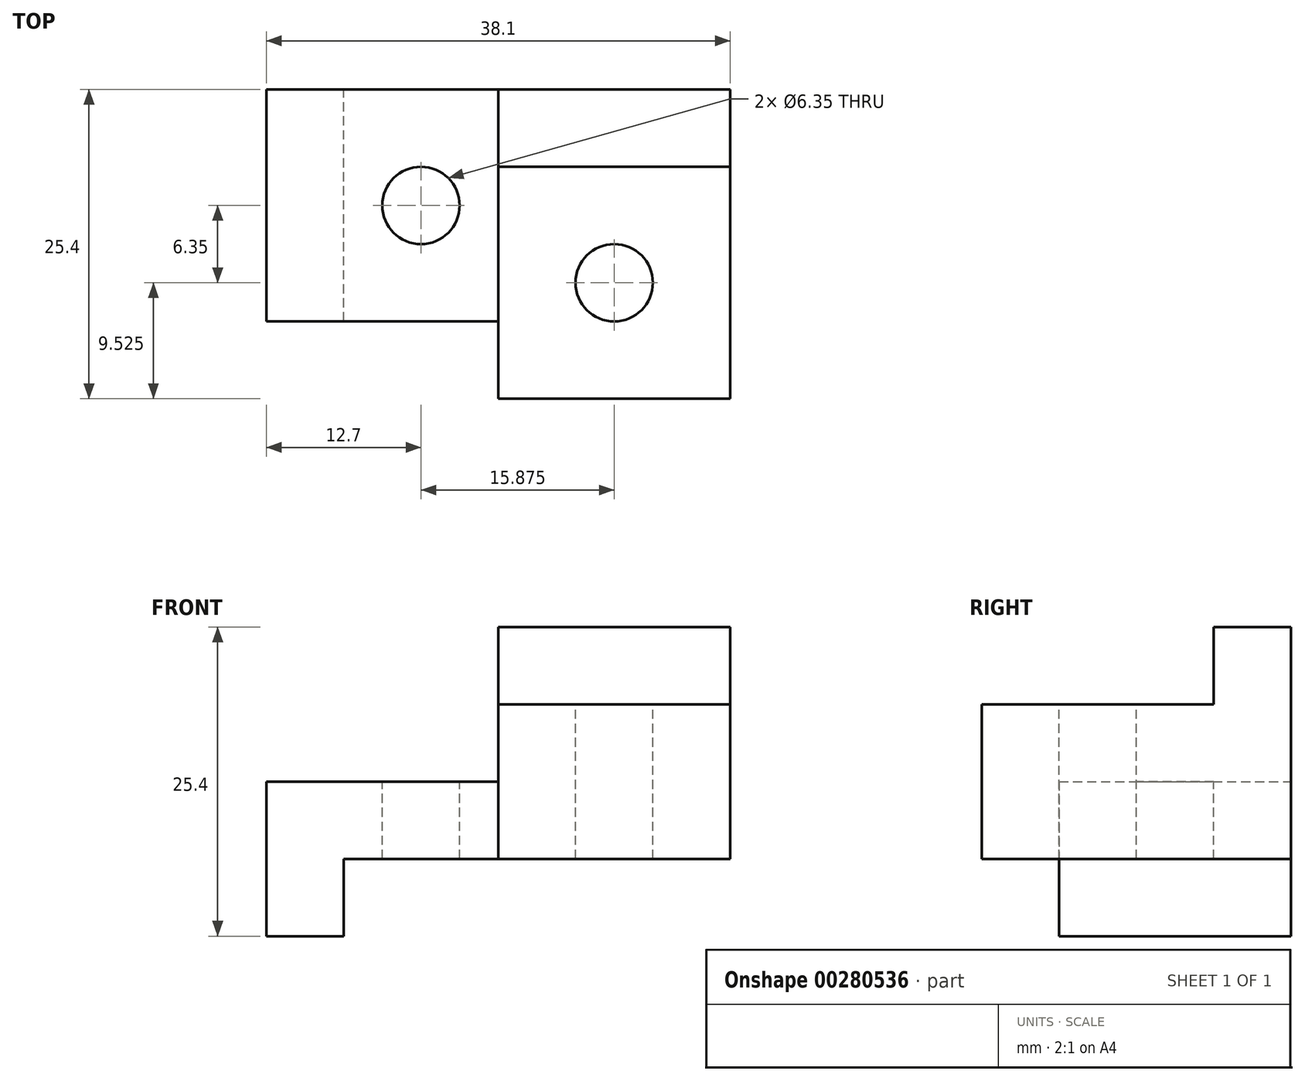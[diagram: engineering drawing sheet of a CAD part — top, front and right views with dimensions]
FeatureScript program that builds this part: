
annotation { "Feature Type Name" : "Feature", "Feature Type Description" : "" }
export const myFeature = defineFeature(function(context is Context, id is Id, definition is map)
    precondition{}
    {
        {
            var Q0;
            Q0=qCreatedBy(makeId("Top.planeOp"),FACE);
            var sketch = newSketch(context, id + "F0", { "sketchPlane" : qUnion([Q0])});
            skLineSegment(sketch, "E0.bottom", {"start": v(0, 0) * mm, "end": v(6.35, 0) * mm});
            skLineSegment(sketch, "E0.top", {"start": v(0, 19.05) * mm, "end": v(6.35, 19.05) * mm});
            skLineSegment(sketch, "E0.left", {"start": v(0, 0) * mm, "end": v(0, 19.05) * mm});
            skLineSegment(sketch, "E0.right", {"start": v(6.35, 0) * mm, "end": v(6.35, 19.05) * mm});
            skSolve(sketch);
        }
        {
            var Q0;
            Q0 = qSketchRegion(id + "F0", true);
            extrude(context, id + "F1", {"entities" : qUnion([Q0]), "depth" : 6.35 * mm});
        }
        {
            var Q0;
            Q0=makeQuery(id+"F1.opExtrude","CAP_FACE",FACE,{"disambiguationData":[OSD([sQuery(id+"F0.wireOp",EDGE,"E0.bottom"),sQuery(id+"F0.wireOp",EDGE,"E0.top"),sQuery(id+"F0.wireOp",EDGE,"E0.left"),sQuery(id+"F0.wireOp",EDGE,"E0.right")])],"isStart":false});
            var sketch = newSketch(context, id + "F2", { "sketchPlane" : qUnion([Q0])});
            skLineSegment(sketch, "E1.bottom", {"start": v(0, 19.05) * mm, "end": v(19.05, 19.05) * mm});
            skLineSegment(sketch, "E1.top", {"start": v(0, 0) * mm, "end": v(19.05, 0) * mm});
            skLineSegment(sketch, "E1.left", {"start": v(0, 19.05) * mm, "end": v(0, 0) * mm});
            skLineSegment(sketch, "E1.right", {"start": v(19.05, 19.05) * mm, "end": v(19.05, 0) * mm});
            skSolve(sketch);
        }
        {
            var Q0;
            Q0 = qSketchRegion(id + "F2", true);
            extrude(context, id + "F3", {"entities" : qUnion([Q0]), "operationType" : NewBodyOperationType.ADD, "depth" : 6.35 * mm});
        }
        {
            var Q0;
            Q0=makeQuery(id+"F3.opExtrude","SWEPT_FACE",FACE,{"disambiguationData":[OSD([sQuery(id+"F2.wireOp",EDGE,"E1.right")])]});
            var sketch = newSketch(context, id + "F4", { "sketchPlane" : qUnion([Q0])});
            skLineSegment(sketch, "E2.bottom", {"start": v(19.05, 6.35) * mm, "end": v(-6.35, 6.35) * mm});
            skLineSegment(sketch, "E2.top", {"start": v(19.05, 25.4) * mm, "end": v(-6.35, 25.4) * mm});
            skLineSegment(sketch, "E2.left", {"start": v(19.05, 6.35) * mm, "end": v(19.05, 25.4) * mm});
            skLineSegment(sketch, "E2.right", {"start": v(-6.35, 6.35) * mm, "end": v(-6.35, 25.4) * mm});
            skSolve(sketch);
        }
        {
            var Q0;
            Q0 = qSketchRegion(id + "F4", true);
            extrude(context, id + "F5", {"entities" : qUnion([Q0]), "operationType" : NewBodyOperationType.ADD, "depth" : 19.05 * mm});
        }
        {
            var Q0;
            Q0=makeQuery(id+"F5.opExtrude","SWEPT_FACE",FACE,{"disambiguationData":[OSD([sQuery(id+"F4.wireOp",EDGE,"E2.top")])]});
            var sketch = newSketch(context, id + "F6", { "sketchPlane" : qUnion([Q0])});
            skLineSegment(sketch, "E3.bottom", {"start": v(38.1, -6.35) * mm, "end": v(19.05, -6.35) * mm});
            skLineSegment(sketch, "E3.top", {"start": v(38.1, 12.7) * mm, "end": v(19.05, 12.7) * mm});
            skLineSegment(sketch, "E3.left", {"start": v(38.1, -6.35) * mm, "end": v(38.1, 12.7) * mm});
            skLineSegment(sketch, "E3.right", {"start": v(19.05, -6.35) * mm, "end": v(19.05, 12.7) * mm});
            skSolve(sketch);
        }
        {
            var Q0;
            Q0 = qSketchRegion(id + "F6", true);
            extrude(context, id + "F7", {"entities" : qUnion([Q0]), "operationType" : NewBodyOperationType.REMOVE, "oppositeDirection" : true, "depth" : 6.35 * mm});
        }
        {
            var Q0;
            Q0=makeQuery(id+"F3.opExtrude","CAP_FACE",FACE,{"disambiguationData":[OSD([sQuery(id+"F2.wireOp",EDGE,"E1.bottom"),sQuery(id+"F2.wireOp",EDGE,"E1.top"),sQuery(id+"F2.wireOp",EDGE,"E1.left"),sQuery(id+"F2.wireOp",EDGE,"E1.right")])],"isStart":false});
            var sketch = newSketch(context, id + "F8", { "sketchPlane" : qUnion([Q0])});
            skCircle(sketch, "E4", {"center": v(12.7, 9.52) * mm, "radius": 3.18 * mm});
            skLineSegment(sketch, "E5", {"start": v(0, 0) * mm, "end": v(12.7, 0) * mm});
            skSolve(sketch);
        }
        {
            var Q0;
            Q0 = qSketchRegion(id + "F8", true);
            extrude(context, id + "F9", {"entities" : qUnion([Q0]), "operationType" : NewBodyOperationType.REMOVE, "oppositeDirection" : true, "depth" : 25.4 * mm});
        }
        {
            var Q0;
            Q0=makeQuery(id+"F7.boolean.opBoolean","COPY",FACE,{"derivedFrom":makeQuery(id+"F7.opExtrude","CAP_FACE",FACE,{"disambiguationData":[OSD([sQuery(id+"F6.wireOp",EDGE,"E3.bottom"),sQuery(id+"F6.wireOp",EDGE,"E3.top"),sQuery(id+"F6.wireOp",EDGE,"E3.left"),sQuery(id+"F6.wireOp",EDGE,"E3.right")])],"isStart":false})});
            var sketch = newSketch(context, id + "F10", { "sketchPlane" : qUnion([Q0])});
            skCircle(sketch, "E6", {"center": v(28.58, 3.17) * mm, "radius": 3.18 * mm});
            skPoint(sketch, "E6.centerSnap0", {"position": v(28.58, -6.35) * mm});
            skSolve(sketch);
        }
        {
            var Q0;
            Q0 = qSketchRegion(id + "F10", true);
            extrude(context, id + "F11", {"entities" : qUnion([Q0]), "operationType" : NewBodyOperationType.REMOVE, "oppositeDirection" : true, "depth" : 25.4 * mm});
        }
    });
